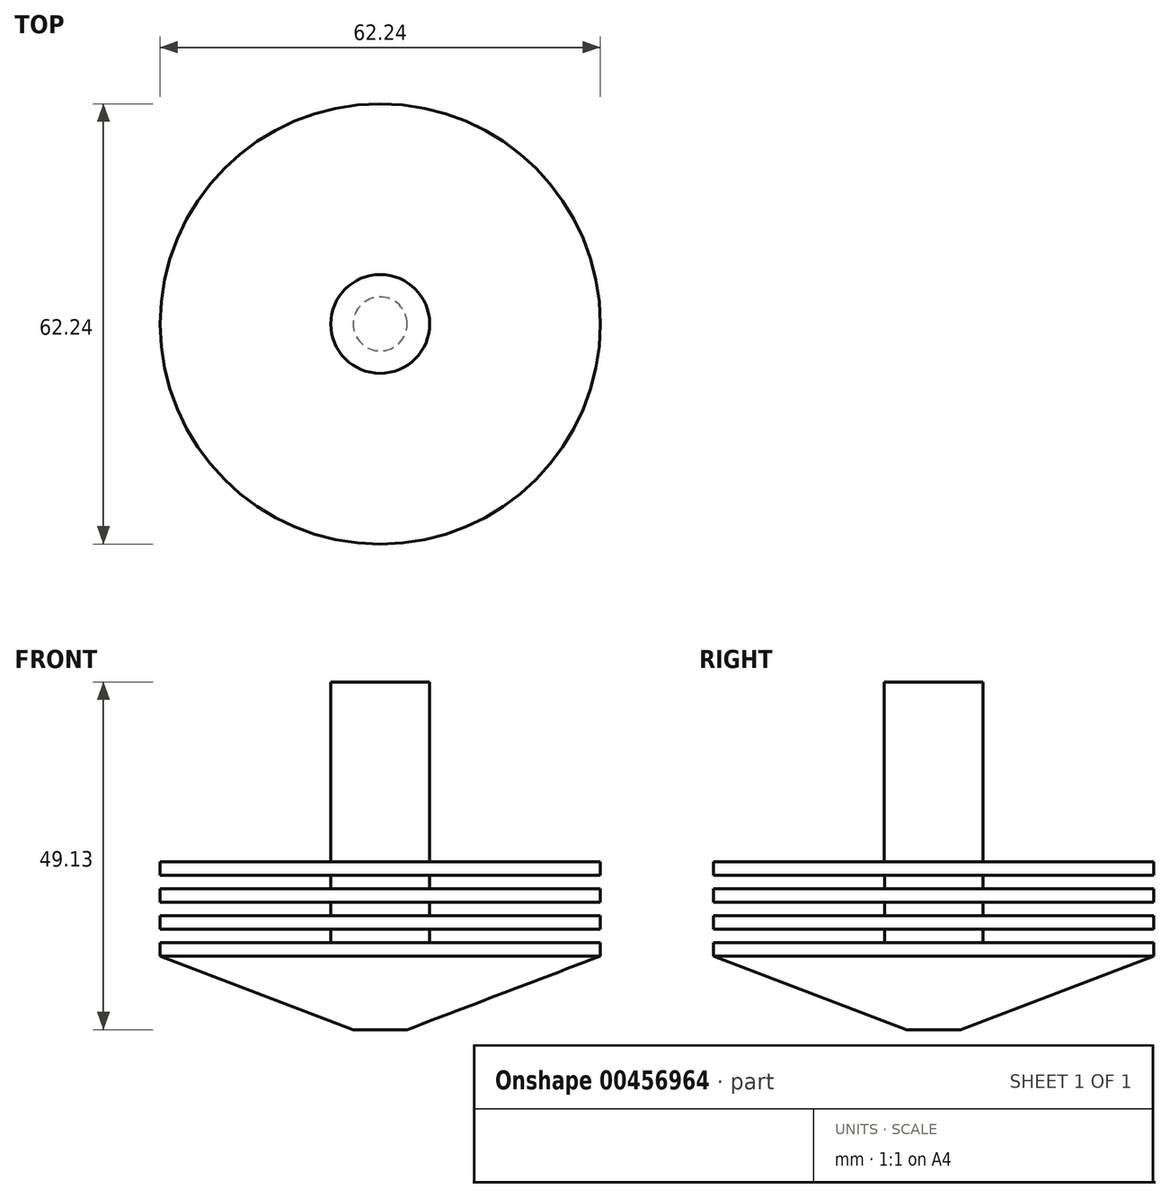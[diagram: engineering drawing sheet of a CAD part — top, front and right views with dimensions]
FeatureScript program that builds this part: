
annotation { "Feature Type Name" : "Feature", "Feature Type Description" : "" }
export const myFeature = defineFeature(function(context is Context, id is Id, definition is map)
    precondition{}
    {
        {
            var Q0;
            Q0=qCreatedBy(makeId("Front.planeOp"),FACE);
            var sketch = newSketch(context, id + "F0", { "sketchPlane" : qUnion([Q0])});
            skLineSegment(sketch, "E0", {"start": v(31.12, 25.62) * mm, "end": v(6.99, 25.62) * mm});
            skLineSegment(sketch, "E1", {"start": v(6.99, 25.62) * mm, "end": v(6.99, 51.02) * mm});
            skLineSegment(sketch, "E2", {"start": v(6.99, 51.02) * mm, "end": v(0, 51.02) * mm});
            skLineSegment(sketch, "E3", {"start": v(0, 51.02) * mm, "end": v(0, 1.89) * mm});
            skLineSegment(sketch, "E4", {"start": v(0, 1.89) * mm, "end": v(3.81, 1.89) * mm});
            skLineSegment(sketch, "E5", {"start": v(3.81, 1.89) * mm, "end": v(31.12, 12.28) * mm});
            skLineSegment(sketch, "E6", {"start": v(31.12, 25.62) * mm, "end": v(31.12, 23.71) * mm});
            skLineSegment(sketch, "E7", {"start": v(31.12, 23.71) * mm, "end": v(6.97, 23.71) * mm});
            skLineSegment(sketch, "E8", {"start": v(6.97, 23.71) * mm, "end": v(6.97, 21.8) * mm});
            skLineSegment(sketch, "E9", {"start": v(6.97, 21.8) * mm, "end": v(31.12, 21.8) * mm});
            skLineSegment(sketch, "E10", {"start": v(31.12, 21.8) * mm, "end": v(31.12, 19.9) * mm});
            skLineSegment(sketch, "E11", {"start": v(31.12, 19.9) * mm, "end": v(6.97, 19.9) * mm});
            skLineSegment(sketch, "E12", {"start": v(6.97, 19.9) * mm, "end": v(6.97, 18) * mm});
            skLineSegment(sketch, "E13", {"start": v(6.97, 18) * mm, "end": v(31.12, 18) * mm});
            skLineSegment(sketch, "E14", {"start": v(31.12, 18) * mm, "end": v(31.12, 16.1) * mm});
            skLineSegment(sketch, "E15", {"start": v(31.12, 16.1) * mm, "end": v(6.97, 16.1) * mm});
            skLineSegment(sketch, "E16", {"start": v(6.97, 16.1) * mm, "end": v(6.97, 14.19) * mm});
            skLineSegment(sketch, "E17", {"start": v(6.97, 14.19) * mm, "end": v(31.12, 14.19) * mm});
            skLineSegment(sketch, "E18", {"start": v(31.12, 14.19) * mm, "end": v(31.12, 12.28) * mm});
            skSolve(sketch);
        }
        {
            var Q0;
            Q0=makeQuery(id+"F0.imprint","IMPRINT",FACE,{"disambiguationData":[TD([[makeQuery(id+"F0.imprint","IMPRINT",EDGE,{"derivedFrom":sQuery(id+"F0.wireOp",EDGE,"E0")}),1.0]])]});
            var Q1;
            Q1=sQuery(id+"F0.wireOp",EDGE,"E3");
            revolve(context, id + "F1", {"entities" : qUnion([Q0]), "axis" : qUnion([Q1]), "revolveType" : RevolveType.FULL});
        }
    });
